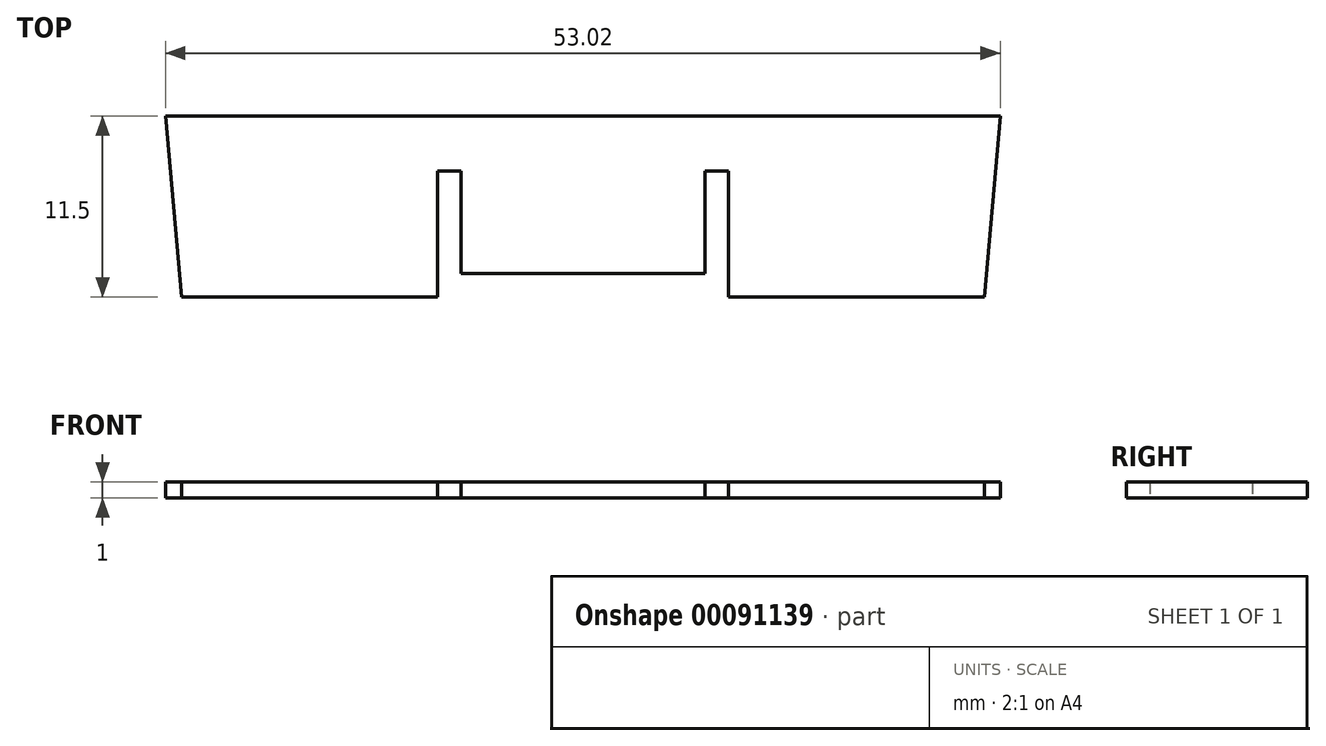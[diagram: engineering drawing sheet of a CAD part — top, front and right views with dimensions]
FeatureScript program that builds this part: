
annotation { "Feature Type Name" : "Feature", "Feature Type Description" : "" }
export const myFeature = defineFeature(function(context is Context, id is Id, definition is map)
    precondition{}
    {
        {
            var Q0;
            Q0=qCreatedBy(makeId("Top.planeOp"),FACE);
            var sketch = newSketch(context, id + "F0", { "sketchPlane" : qUnion([Q0])});
            skLineSegment(sketch, "E0.bottom", {"start": v(-25.5, 5.75) * mm, "end": v(25.5, 5.75) * mm});
            skLineSegment(sketch, "E0.top", {"start": v(-25.5, -5.75) * mm, "end": v(25.5, -5.75) * mm});
            skLineSegment(sketch, "E0.left", {"start": v(-25.5, 5.75) * mm, "end": v(-25.5, -5.75) * mm});
            skLineSegment(sketch, "E0.right", {"start": v(25.5, 5.75) * mm, "end": v(25.5, -5.75) * mm});
            skPoint(sketch, "E0.middle", {"position": v(0, 0) * mm});
            skLineSegment(sketch, "E1.bottom", {"start": v(-9.25, -5.75) * mm, "end": v(-7.75, -5.75) * mm});
            skLineSegment(sketch, "E1.top", {"start": v(-9.25, 2.25) * mm, "end": v(-7.75, 2.25) * mm});
            skLineSegment(sketch, "E1.left", {"start": v(-9.25, -5.75) * mm, "end": v(-9.25, 2.25) * mm});
            skLineSegment(sketch, "E1.right", {"start": v(-7.75, -5.75) * mm, "end": v(-7.75, 2.25) * mm});
            skLineSegment(sketch, "E2.bottom", {"start": v(7.75, -5.75) * mm, "end": v(9.25, -5.75) * mm});
            skLineSegment(sketch, "E2.top", {"start": v(7.75, 2.25) * mm, "end": v(9.25, 2.25) * mm});
            skLineSegment(sketch, "E2.left", {"start": v(7.75, -5.75) * mm, "end": v(7.75, 2.25) * mm});
            skLineSegment(sketch, "E2.right", {"start": v(9.25, -5.75) * mm, "end": v(9.25, 2.25) * mm});
            skLineSegment(sketch, "E3", {"start": v(-25.5, -5.75) * mm, "end": v(-26.5, 5.75) * mm});
            skLineSegment(sketch, "E4", {"start": v(-26.5, 5.75) * mm, "end": v(-25.5, 5.75) * mm});
            skLineSegment(sketch, "E5", {"start": v(25.5, 5.75) * mm, "end": v(26.5, 5.75) * mm});
            skLineSegment(sketch, "E6", {"start": v(26.5, 5.75) * mm, "end": v(25.5, -5.75) * mm});
            skLineSegment(sketch, "E7", {"start": v(-7.75, -4.25) * mm, "end": v(7.75, -4.25) * mm});
            skSolve(sketch);
        }
        {
            var Q0;
            Q0=makeQuery(id+"F0.imprint","IMPRINT",FACE,{"disambiguationData":[TD([[makeQuery(id+"F0.imprint","IMPRINT",EDGE,{"derivedFrom":sQuery(id+"F0.wireOp",EDGE,"E0.left")}),-1.0]])]});
            var Q1;
            Q1=makeQuery(id+"F0.imprint","IMPRINT",FACE,{"disambiguationData":[TD([[makeQuery(id+"F0.imprint","IMPRINT",EDGE,{"derivedFrom":sQuery(id+"F0.wireOp",EDGE,"E0.bottom")}),-1.0]])]});
            var Q2;
            Q2=makeQuery(id+"F0.imprint","IMPRINT",FACE,{"disambiguationData":[TD([[makeQuery(id+"F0.imprint","IMPRINT",EDGE,{"derivedFrom":sQuery(id+"F0.wireOp",EDGE,"E0.right")}),1.0]])]});
            extrude(context, id + "F1", {"entities" : qUnion([Q0, Q1, Q2]), "depth" : 1 * mm});
        }
    });
